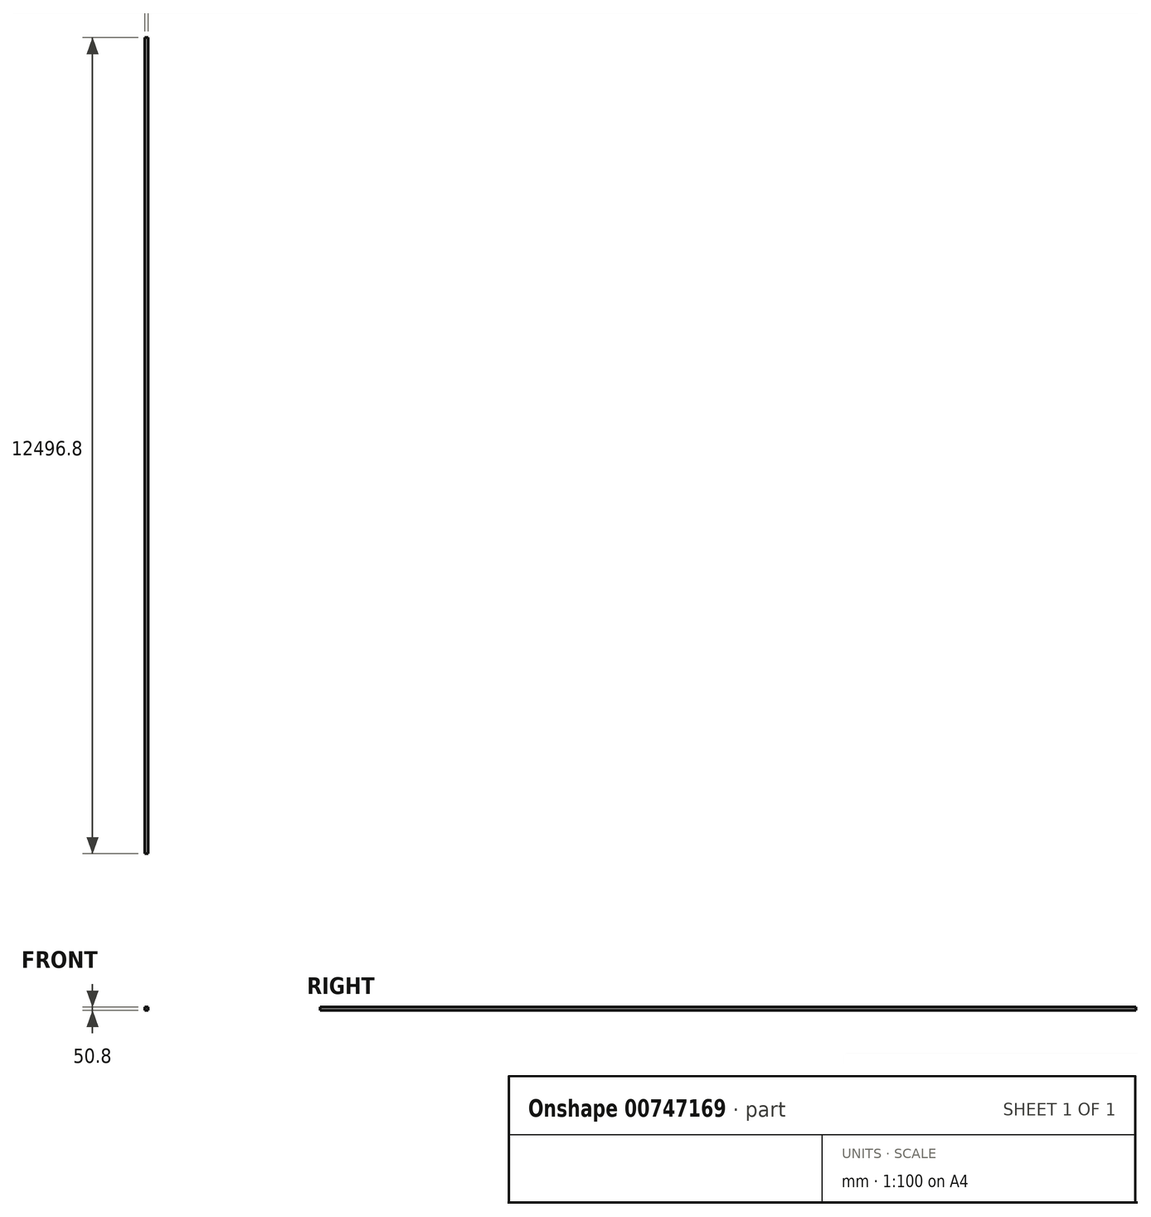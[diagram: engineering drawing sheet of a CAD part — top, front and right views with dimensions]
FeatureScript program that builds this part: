
annotation { "Feature Type Name" : "Feature", "Feature Type Description" : "" }
export const myFeature = defineFeature(function(context is Context, id is Id, definition is map)
    precondition{}
    {
        {
            var Q0;
            Q0=qCreatedBy(makeId("Front.planeOp"),FACE);
            var sketch = newSketch(context, id + "F0", { "sketchPlane" : qUnion([Q0])});
            skLineSegment(sketch, "E0.bottom", {"start": v(-85.12, 74.65) * mm, "end": v(-34.32, 74.65) * mm});
            skLineSegment(sketch, "E0.top", {"start": v(-85.12, 23.85) * mm, "end": v(-34.32, 23.85) * mm});
            skLineSegment(sketch, "E0.left", {"start": v(-85.12, 74.65) * mm, "end": v(-85.12, 23.85) * mm});
            skLineSegment(sketch, "E0.right", {"start": v(-34.32, 74.65) * mm, "end": v(-34.32, 23.85) * mm});
            skSolve(sketch);
        }
        {
            var Q0;
            Q0 = qSketchRegion(id + "F0", true);
            extrude(context, id + "F1", {"entities" : qUnion([Q0]), "depth" : 12496.8 * mm, "offsetDistance" : 25.4 * mm});
        }
    });
